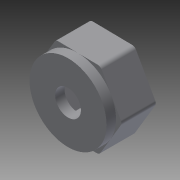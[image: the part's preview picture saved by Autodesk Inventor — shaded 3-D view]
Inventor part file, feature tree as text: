
AUTODESK INVENTOR PART (.ipt)
format: ipt  version: 2014 (Build 180170000, 170)  size: 124,928 bytes
history: native  units: in
note: dims shown in document units (in); Inventor stores cm internally (conversion verified against a paired STEP export)
features: reference x6, extrude x2, sketch x2, fillet x1
ambient origin geometry x8: Origin, YZ Plane, XZ Plane, XY Plane, X Axis, Y Axis, Z Axis, Center Point
bodies: Solid1 (feature_tree)
feature tree (11):
  extrude  "Extrusion1"  Depth=0.315in TaperAngle=0.0deg
  extrude  "Extrusion2"  Depth=0.0866in TaperAngle=0.0deg
  fillet  "Fillet1"  Radius=0.0394in
  sketch  "Sketch2"  dims[d0=0.1181in d1=0.315in d2=0.0in]
  reference  "Reference1"
  reference  "Reference2"
  reference  "Reference3"
  reference  "Reference4"
  reference  "Reference5"
  reference  "Reference6"
  sketch  "Sketch3"  dims[d3=0.2362in d4=0.0866in d5=0.0in d6=0.0394in]
